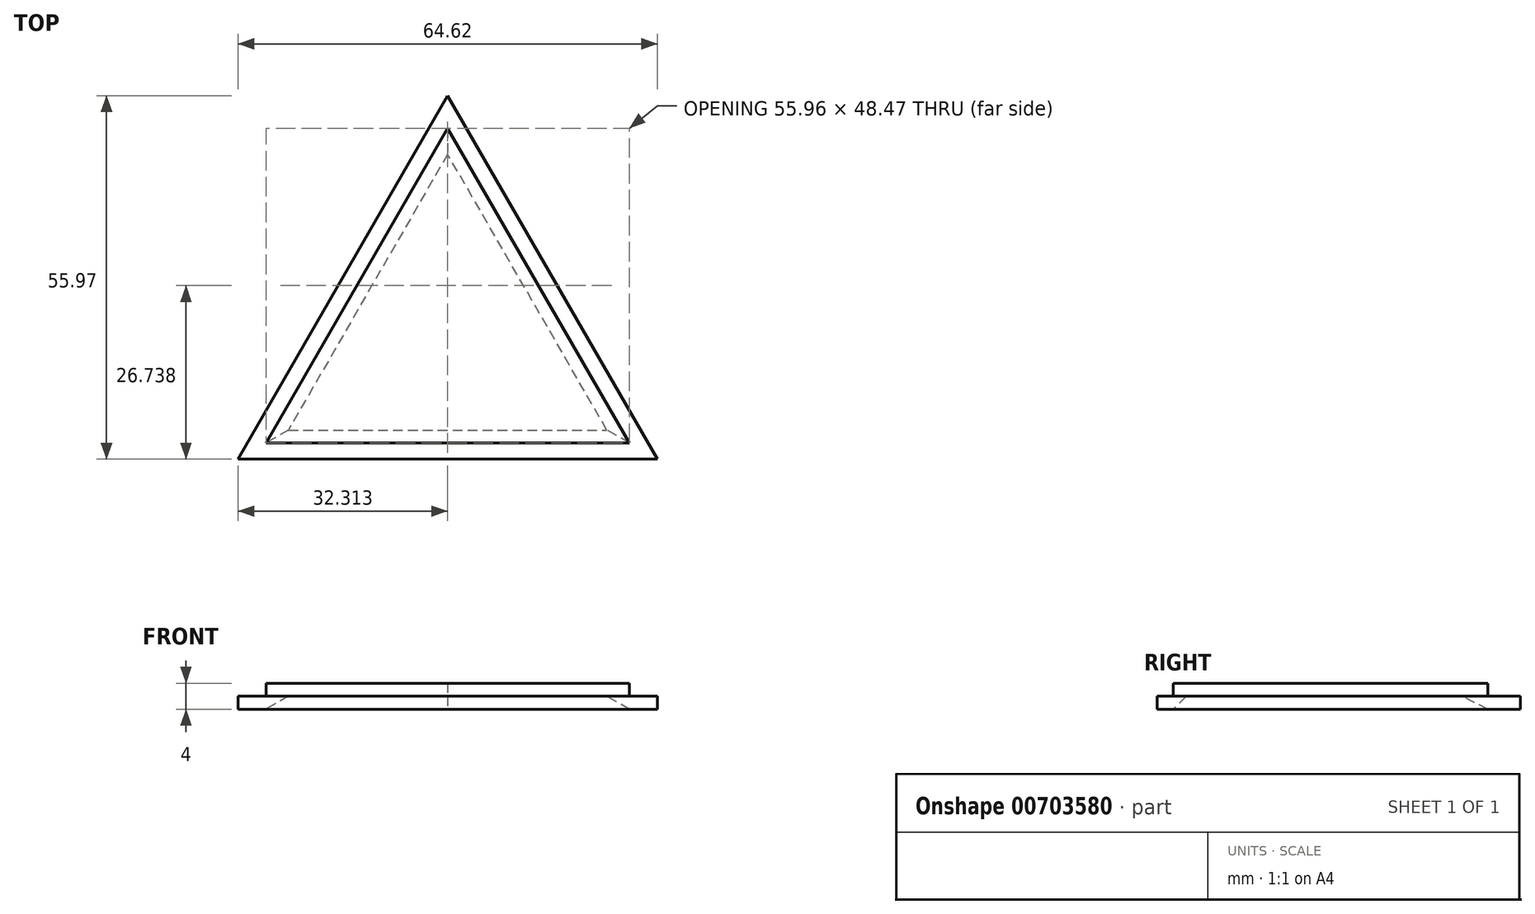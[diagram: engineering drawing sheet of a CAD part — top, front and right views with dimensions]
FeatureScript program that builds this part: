
annotation { "Feature Type Name" : "Feature", "Feature Type Description" : "" }
export const myFeature = defineFeature(function(context is Context, id is Id, definition is map)
    precondition{}
    {
        {
            var Q0;
            Q0=qCreatedBy(makeId("Top.planeOp"),FACE);
            var sketch = newSketch(context, id + "F0", { "sketchPlane" : qUnion([Q0])});
            skLineSegment(sketch, "E0", {"start": v(4.8, 63.3) * mm, "end": v(-23.18, 14.82) * mm});
            skLineSegment(sketch, "E1", {"start": v(-23.18, 14.82) * mm, "end": v(32.78, 14.82) * mm});
            skLineSegment(sketch, "E2", {"start": v(32.78, 14.82) * mm, "end": v(4.8, 63.3) * mm});
            skLineSegment(sketch, "E3", {"start": v(4.8, 68.3) * mm, "end": v(-27.5, 12.32) * mm});
            skLineSegment(sketch, "E4", {"start": v(-27.5, 12.32) * mm, "end": v(37.11, 12.32) * mm});
            skLineSegment(sketch, "E5", {"start": v(37.11, 12.32) * mm, "end": v(4.8, 68.3) * mm});
            skLineSegment(sketch, "E6", {"start": v(4.8, 59.3) * mm, "end": v(-19.72, 16.82) * mm});
            skLineSegment(sketch, "E7", {"start": v(-19.72, 16.82) * mm, "end": v(29.32, 16.82) * mm});
            skLineSegment(sketch, "E8", {"start": v(29.32, 16.82) * mm, "end": v(4.8, 59.3) * mm});
            skSolve(sketch);
        }
        {
            var Q0;
            Q0=makeQuery(id+"F0.imprint","IMPRINT",FACE,{"disambiguationData":[TD([[makeQuery(id+"F0.imprint","IMPRINT",EDGE,{"derivedFrom":sQuery(id+"F0.wireOp",EDGE,"E0")}),1.0]])]});
            extrude(context, id + "F1", {"entities" : qUnion([Q0]), "depth" : 4 * mm, "offsetDistance" : 25 * mm});
        }
        {
            var Q0;
            Q0=makeQuery(id+"F0.imprint","IMPRINT",FACE,{"disambiguationData":[TD([[makeQuery(id+"F0.imprint","IMPRINT",EDGE,{"derivedFrom":sQuery(id+"F0.wireOp",EDGE,"E0")}),-1.0]])]});
            extrude(context, id + "F2", {"entities" : qUnion([Q0]), "operationType" : NewBodyOperationType.ADD, "depth" : 2 * mm, "offsetDistance" : 25 * mm});
        }
        {
            var Q0;
            Q0=makeQuery(id+"F0.imprint","IMPRINT",FACE,{"disambiguationData":[TD([[makeQuery(id+"F0.imprint","IMPRINT",EDGE,{"derivedFrom":sQuery(id+"F0.wireOp",EDGE,"E6")}),1.0]])]});
            extrude(context, id + "F3", {"entities" : qUnion([Q0]), "operationType" : NewBodyOperationType.ADD, "depth" : 4 * mm, "offsetDistance" : 25 * mm, "hasSecondDirection" : true, "secondDirectionOppositeDirection" : true, "secondDirectionDepth" : -2 * mm});
        }
        {
            var Q0;
            Q0=makeQuery(id+"F1.opExtrude","CAP_EDGE",EDGE,{"disambiguationData":[OSD([sQuery(id+"F0.wireOp",EDGE,"E7")])],"isStart":true});
            var Q1;
            Q1=makeQuery(id+"F1.opExtrude","CAP_EDGE",EDGE,{"disambiguationData":[OSD([sQuery(id+"F0.wireOp",EDGE,"E6")])],"isStart":true});
            var Q2;
            Q2=makeQuery(id+"F1.opExtrude","CAP_EDGE",EDGE,{"disambiguationData":[OSD([sQuery(id+"F0.wireOp",EDGE,"E8")])],"isStart":true});
            chamfer(context, id + "F4", {"entities" : qUnion([Q0, Q1, Q2]), "width" : 2 * mm, "tangentPropagation" : true});
        }
    });
